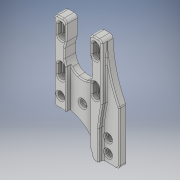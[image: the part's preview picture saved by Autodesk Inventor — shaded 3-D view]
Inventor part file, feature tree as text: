
AUTODESK INVENTOR PART (.ipt)
format: ipt  version: 2018 (Build 220112000, 112)  size: 542,208 bytes
history: native  units: in
note: dims shown in document units (in); Inventor stores cm internally (conversion verified against a paired STEP export)
features: extrude x12, sketch x12, projected_geometry x4, fillet x3, plane x2, chamfer x1
ambient origin geometry x8: Origin, YZ Plane, XZ Plane, XY Plane, X Axis, Y Axis, Z Axis, Center Point
bodies: Solid1 (feature_tree)
feature tree (34):
  extrude  "Extrusion1"  Depth=1.6929in
  extrude  "Extrusion2"  Depth=0.4331in
  fillet  "Fillet1"  Radius=1.6535in
  extrude  "Extrusion3"  Depth=1.2205in
  extrude  "Extrusion4"  Depth=0.126in
  extrude  "Extrusion5"  Depth=0.315in
  extrude  "Extrusion6"  Depth=0.2362in TaperAngle=0.0deg
  plane  "Work Plane1"
  plane  "Work Plane2"
  extrude  "Extrusion7"  Depth=0.1575in TaperAngle=0.0deg
  extrude  "Extrusion8"  Depth=0.2362in
  extrude  "Extrusion9"  Depth=0.9449in
  extrude  "Extrusion10"  Depth=0.6102in
  extrude  "Extrusion11"  Depth=1.2992in
  extrude  "Extrusion12"  Depth=0.1181in
  fillet  "Fillet2"  Radius=7.0866in
  fillet  "Fillet4"  Radius=0.2362in
  chamfer  "Chamfer1"  Distance=0.1654in
  sketch  "Sketch1"  dims[d0=3.8189in d1=1.6929in]
  sketch  "Sketch2"  dims[d2=0.4331in d3=0.4331in d4=1.6535in]
  sketch  "Sketch3"  dims[d5=0.2362in d6=0.0in d7=1.2205in]
  projected_geometry  "Projected Loop1"
  sketch  "Sketch4"  dims[d8=1.2205in d9=0.126in]
  projected_geometry  "Projected Loop2"
  sketch  "Sketch5"  dims[d10=0.2756in d11=0.315in]
  projected_geometry  "Projected Loop3"
  sketch  "Sketch6"  dims[d12=0.315in d13=0.2362in d14=0.0in]
  sketch  "Sketch8"  dims[d15=0.315in d16=0.1575in d17=0.0in]
  sketch  "Sketch9"  dims[d18=0.2362in d20=0.2362in]
  sketch  "Sketch10"  dims[d21=0.1575in d22=0.0in d23=0.9449in]
  projected_geometry  "Projected Loop4"
  sketch  "Sketch11"  dims[d24=0.315in d25=0.6102in]
  sketch  "Sketch12"  dims[d26=0.0in d27=0.0in d28=1.2992in]
  sketch  "Sketch13"  dims[d30=0.2362in d31=0.0in d32=0.1181in d33=7.0866in d34=0.2362in d35=0.0in d36=0.1654in d38=0.3937in d39=0.315in d40=0.4724in d41=0.2362in d42=0.0in d43=0.2165in d44=0.1654in d46=0.2165in d47=0.3937in d50=0.2362in d51=0.0in d52=0.2441in d53=0.0787in d54=0.0in d55=0.0787in d56=0.0in d57=0.7874in d58=0.3937in d59=0.7874in d60=0.0in d61=0.7874in d62=0.0in d63=0.1181in d65=0.0394in d66=0.0394in d67=0.0787in d68=45.0deg d69=1.063in]
